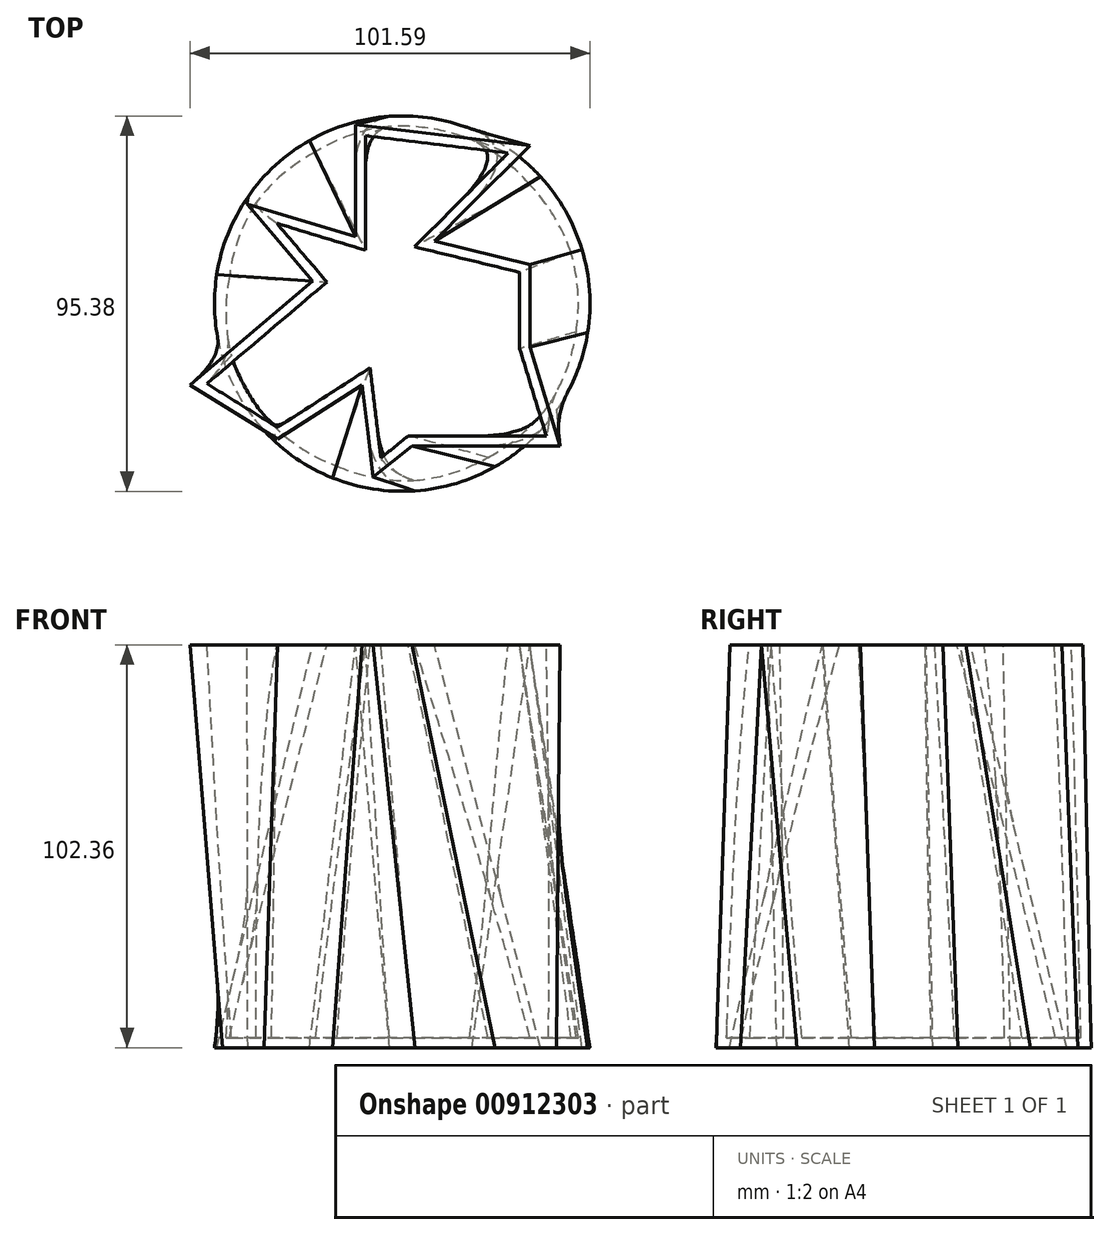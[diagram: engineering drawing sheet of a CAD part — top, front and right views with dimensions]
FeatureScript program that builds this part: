
annotation { "Feature Type Name" : "Feature", "Feature Type Description" : "" }
export const myFeature = defineFeature(function(context is Context, id is Id, definition is map)
    precondition{}
    {
        {
            var Q0;
            Q0=qCreatedBy(makeId("Top.planeOp"),FACE);
            var sketch = newSketch(context, id + "F0", { "sketchPlane" : qUnion([Q0])});
            skCircle(sketch, "E0", {"center": v(-2.48, 0) * mm, "radius": 47.69 * mm});
            skSolve(sketch);
        }
        {
            var Q0;
            Q0=makeQuery(id+"F0.imprint","IMPRINT",FACE,{"disambiguationData":[TD([[makeQuery(id+"F0.imprint","IMPRINT",EDGE,{"derivedFrom":sQuery(id+"F0.wireOp",EDGE,"E0")}),1.0]])]});
            cPlane(context, id + "F1", {"entities" : qUnion([Q0]), "cplaneType" : CPlaneType.OFFSET, "offset" : 102.36 * mm, "width" : 152.4 * mm, "height" : 152.4 * mm});
        }
        {
            var Q0;
            Q0=qCreatedBy(id+"F1.planeOp",FACE);
            var sketch = newSketch(context, id + "F2", { "sketchPlane" : qUnion([Q0])});
            skLineSegment(sketch, "E1", {"start": v(0, -36.15) * mm, "end": v(37.54, -36.15) * mm});
            skLineSegment(sketch, "E2", {"start": v(37.54, -36.15) * mm, "end": v(29.92, -11.03) * mm});
            skLineSegment(sketch, "E3", {"start": v(29.92, -11.03) * mm, "end": v(29.92, 9.94) * mm});
            skLineSegment(sketch, "E4", {"start": v(29.92, 9.94) * mm, "end": v(5.68, 15.88) * mm});
            skLineSegment(sketch, "E5", {"start": v(5.68, 15.88) * mm, "end": v(29.92, 40.17) * mm});
            skLineSegment(sketch, "E6", {"start": v(29.92, 40.17) * mm, "end": v(-14.35, 45.5) * mm});
            skLineSegment(sketch, "E7", {"start": v(-14.35, 45.5) * mm, "end": v(-14.35, 17.03) * mm});
            skLineSegment(sketch, "E8", {"start": v(-14.35, 17.03) * mm, "end": v(-41.88, 25.32) * mm});
            skLineSegment(sketch, "E9", {"start": v(-41.88, 25.32) * mm, "end": v(-25.26, 5.77) * mm});
            skLineSegment(sketch, "E10", {"start": v(-25.26, 5.77) * mm, "end": v(-56.38, -20.69) * mm});
            skLineSegment(sketch, "E11", {"start": v(-56.38, -20.69) * mm, "end": v(-34.17, -34.45) * mm});
            skLineSegment(sketch, "E12", {"start": v(-34.17, -34.45) * mm, "end": v(-12.7, -20.69) * mm});
            skLineSegment(sketch, "E13", {"start": v(-12.7, -20.69) * mm, "end": v(-9.86, -44.11) * mm});
            skLineSegment(sketch, "E14", {"start": v(-9.86, -44.11) * mm, "end": v(0, -36.15) * mm});
            skSolve(sketch);
        }
        {
            var Q0;
            Q0=makeQuery(id+"F0.imprint","IMPRINT",FACE,{"disambiguationData":[TD([[makeQuery(id+"F0.imprint","IMPRINT",EDGE,{"derivedFrom":sQuery(id+"F0.wireOp",EDGE,"E0")}),1.0]])]});
            var Q1;
            Q1=makeQuery(id+"F2.imprint","IMPRINT",FACE,{"disambiguationData":[TD([[makeQuery(id+"F2.imprint","IMPRINT",EDGE,{"derivedFrom":sQuery(id+"F2.wireOp",EDGE,"E1")}),1.0]])]});
            loft(context, id + "F3", {"sheetProfilesArray" : [{ "sheetProfileEntities" : qUnion([Q0]) }, { "sheetProfileEntities" : qUnion([Q1]) }]});
        }
        {
            var Q0;
            Q0=makeQuery(id+"F3.opLoft","CAP_FACE",FACE,{"disambiguationData":[OSD([makeQuery(id+"F2.imprint","IMPRINT",FACE,{"disambiguationData":[TD([[makeQuery(id+"F2.imprint","IMPRINT",EDGE,{"derivedFrom":sQuery(id+"F2.wireOp",EDGE,"E1")}),1.0]])]})])],"isStart":true});
            shell(context, id + "F4", {"entities" : qUnion([Q0]), "thickness" : 2.54 * mm});
        }
    });
